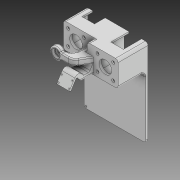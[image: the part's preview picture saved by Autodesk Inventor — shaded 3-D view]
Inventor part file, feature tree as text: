
AUTODESK INVENTOR PART (.ipt)
format: ipt  version: 2020 (Build 240168000, 168)  size: 774,144 bytes
history: native  units: mm
features: sketch x22, extrude x21, projected_geometry x5, plane x4, fillet x3, revolve x2, chamfer x1
ambient origin geometry x8: Origin, YZ Plane, XZ Plane, XY Plane, X Axis, Y Axis, Z Axis, Center Point
bodies: Solid1 (feature_tree)
feature tree (58):
  extrude  "Extrusion1"  Depth=120.0mm
  extrude  "Extrusion2"  Depth=55.0mm TaperAngle=0.0deg
  extrude  "Extrusion3"  Depth=44.0mm
  extrude  "Extrusion4"  Depth=25.0mm
  extrude  "Extrusion5"  Depth=25.0mm TaperAngle=0.0deg
  extrude  "Extrusion6"  Depth=3.5mm
  extrude  "Extrusion7"  TaperAngle=0.0deg  [1 undecoded]
  extrude  "Extrusion8"  Depth=21.0mm TaperAngle=0.0deg
  extrude  "Extrusion9"  Depth=14.0mm TaperAngle=0.0deg
  extrude  "Extrusion10"  Depth=2.5mm TaperAngle=0.0deg
  extrude  "Extrusion11"  Depth=2.5mm TaperAngle=0.0deg
  extrude  "Extrusion13"  Depth=44.0mm
  extrude  "Extrusion15"  Depth=3.0mm
  extrude  "Extrusion16"  Depth=3.0mm
  extrude  "Extrusion17"  Depth=28.0mm
  chamfer  "Chamfer2"  Distance=25.0mm
  plane  "Work Plane1"
  extrude  "Extrusion18"  Depth=25.0mm TaperAngle=0.0deg
  extrude  "Extrusion19"  Depth=12.5mm
  plane  "Work Plane2"
  sketch  "Sketch25"  dims[d69=72.0mm d70=3.621558mm d71=3.621558mm d72=5.0mm d73=3.5mm]
  revolve  "Revolution1"  [1 undecoded]
  revolve  "Revolution2"  [1 undecoded]
  fillet  "Fillet3"  Radius=3.621558mm
  fillet  "Fillet4"  Radius=5.0mm
  fillet  "Fillet5"  Radius=3.5mm
  extrude  "Extrusion22"  Depth=9.0mm
  extrude  "Extrusion23"  Depth=4.0mm
  plane  "Work Plane3"
  plane  "Work Plane4"
  extrude  "Extrusion24"  Depth=8.0mm
  extrude  "Extrusion25"  Depth=8.0mm
  sketch  "Sketch1"  dims[d1=122.0mm d3=120.0mm]
  sketch  "Sketch2"  dims[d4=4.0mm d5=0.0mm d6=55.0mm d7=0.0mm]
  sketch  "Sketch3"  dims[d8=44.0mm d9=44.0mm]
  sketch  "Sketch4"  dims[d10=44.0mm d11=25.0mm]
  sketch  "Sketch5"  dims[d12=25.0mm d14=20.0mm d15=0.0mm]
  sketch  "Sketch6"  dims[d16=31.0mm d17=3.5mm]
  sketch  "Sketch7"  dims[d18=25.0mm d19=0.0mm d20=0.0mm]
  projected_geometry  "Projected Loop1"
  sketch  "Sketch8"  dims[d21=25.0mm d22=21.0mm d23=0.0mm]
  sketch  "Sketch9"  dims[d24=14.0mm d25=0.0mm d26=14.0mm d27=0.0mm]
  sketch  "Sketch10"  dims[d28=6.0mm d29=2.5mm d30=0.0mm]
  sketch  "Sketch11"  dims[d31=6.0mm d32=2.5mm d33=0.0mm]
  sketch  "Sketch13"  dims[d35=44.0mm d36=44.0mm]
  sketch  "Sketch15"  dims[d37=3.0mm d38=3.0mm]
  sketch  "Sketch17"  dims[d39=25.0mm d40=3.0mm]
  projected_geometry  "Projected Loop2"
  sketch  "Sketch18"  dims[d41=3.0mm d42=28.0mm]
  sketch  "Sketch19"  dims[d44=22.0mm d45=25.0mm d46=0.0mm]
  sketch  "Sketch20"  dims[d47=21.0mm d51=25.0mm d52=0.0mm]
  sketch  "Sketch23"  dims[d53=12.5mm d59=2.4mm d60=12.5mm d61=20.5mm]
  sketch  "Sketch24"  dims[d64=90.974mm d65=0.0mm d68=72.0mm]
  projected_geometry  "Projected Loop3"
  sketch  "Sketch26"  dims[d77=2.0mm d78=9.0mm]
  projected_geometry  "Projected Loop4"
  sketch  "Sketch27"  dims[d79=22.68928mm d80=20.0mm d81=8.0mm d82=8.0mm d83=8.0mm d84=32.0mm d85=9.0mm d86=1.5mm d87=0.0mm d93=15.0mm d94=0.0mm d95=8.0mm d96=2.0mm d97=3.0mm d98=0.0mm d99=0.5mm d100=2.0mm d101=45.0deg d103=31.0mm d105=9.0mm d106=150.0deg d107=15.0deg d108=5.0mm d109=12.0mm d110=0.0mm d111=5.3mm d112=0.0mm d113=0.0mm d117=3.0mm d121=15.0mm d122=7.0mm d123=12.0mm d125=5.0mm d126=2.0mm d127=8.0mm d128=141.0mm d129=21.0mm d130=15.0mm d131=15.0mm d132=15.0mm d133=15.0mm d134=10.0mm d135=12.0mm d136=2.5mm d137=0.0mm d138=10.0mm d139=0.0mm d141=8.125mm d142=3.5mm d143=90.0deg d144=90.0deg d145=2.0mm d146=0.5mm d147=5.0mm d148=4.0mm d149=0.5mm d150=-5.0mm d151=-5.0mm d152=20.0mm d153=0.0mm d154=20.0mm d155=0.0mm]
  projected_geometry  "Projected Loop5"
note: 3 required parameter values undecoded (feature->parameter linkage not recoverable at this tier; creation-order binding heuristic only, values carry confidence <= 0.55)